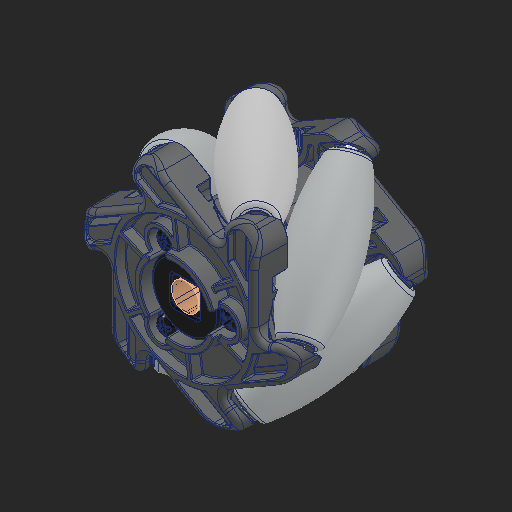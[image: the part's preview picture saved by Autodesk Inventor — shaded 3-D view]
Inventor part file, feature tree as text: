
AUTODESK INVENTOR PART (.ipt)
format: ipt  version: 2023 (Build 270158000, 158)  size: 35,798,016 bytes
history: native  units: in
note: dims shown in document units (in); Inventor stores cm internally (conversion verified against a paired STEP export)
features: other x35, sketch x1, extrude x1
ambient origin geometry x8: Origin, YZ Plane, XZ Plane, XY Plane, X Axis, Y Axis, Z Axis, Center Point
bodies: Solid2 (feature_tree), Solid3 (feature_tree), Solid4 (feature_tree), Solid5 (feature_tree), Solid7 (feature_tree), Solid8 (feature_tree), Solid9 (feature_tree), Solid10 (feature_tree), Solid12 (feature_tree), Solid13 (feature_tree), Solid14 (feature_tree), Solid15 (feature_tree), Solid17 (feature_tree), Solid18 (feature_tree), Solid19 (feature_tree), Solid20 (feature_tree), Solid22 (feature_tree), Solid23 (feature_tree), Solid24 (feature_tree), Solid25 (feature_tree), Solid27 (feature_tree), Solid28 (feature_tree), Solid29 (feature_tree), Solid30 (feature_tree), Solid31 (feature_tree), Solid32 (feature_tree), Solid33 (feature_tree), Solid34 (feature_tree), Solid35 (feature_tree), Solid36 (feature_tree), Solid37 (feature_tree), Solid38 (feature_tree), Solid39 (feature_tree), Solid40 (feature_tree)
feature tree (37):
  sketch  "Sketch1"  dims[d0=1.0in d1=0.0in]
  other  "Srf1"
  other  "NONE:1"
  other  "NONE:2"
  other  "NONE:3"
  other  "NONE:4"
  other  "NONE:6"
  other  "NONE:7"
  other  "NONE:8"
  other  "NONE:9"
  other  "NONE:11"
  other  "NONE:12"
  other  "NONE:13"
  other  "NONE:14"
  other  "NONE:16"
  other  "NONE:17"
  other  "NONE:18"
  other  "NONE:19"
  other  "NONE:21"
  other  "NONE:22"
  other  "NONE:23"
  other  "NONE:24"
  other  "NONE:26"
  other  "NONE:27"
  other  "NONE:28"
  other  "NONE:29"
  other  "NONE:30"
  other  "NONE:31"
  other  "NONE:32"
  other  "NONE:33"
  other  "NONE:34"
  other  "NONE:35"
  other  "NONE:36"
  other  "NONE:37"
  other  "NONE:38"
  other  "NONE:39"
  extrude  "ExtrusionSrf1"  [1 undecoded]
note: 1 required parameter value undecoded (feature->parameter linkage not recoverable at this tier; creation-order binding heuristic only, values carry confidence <= 0.55)
